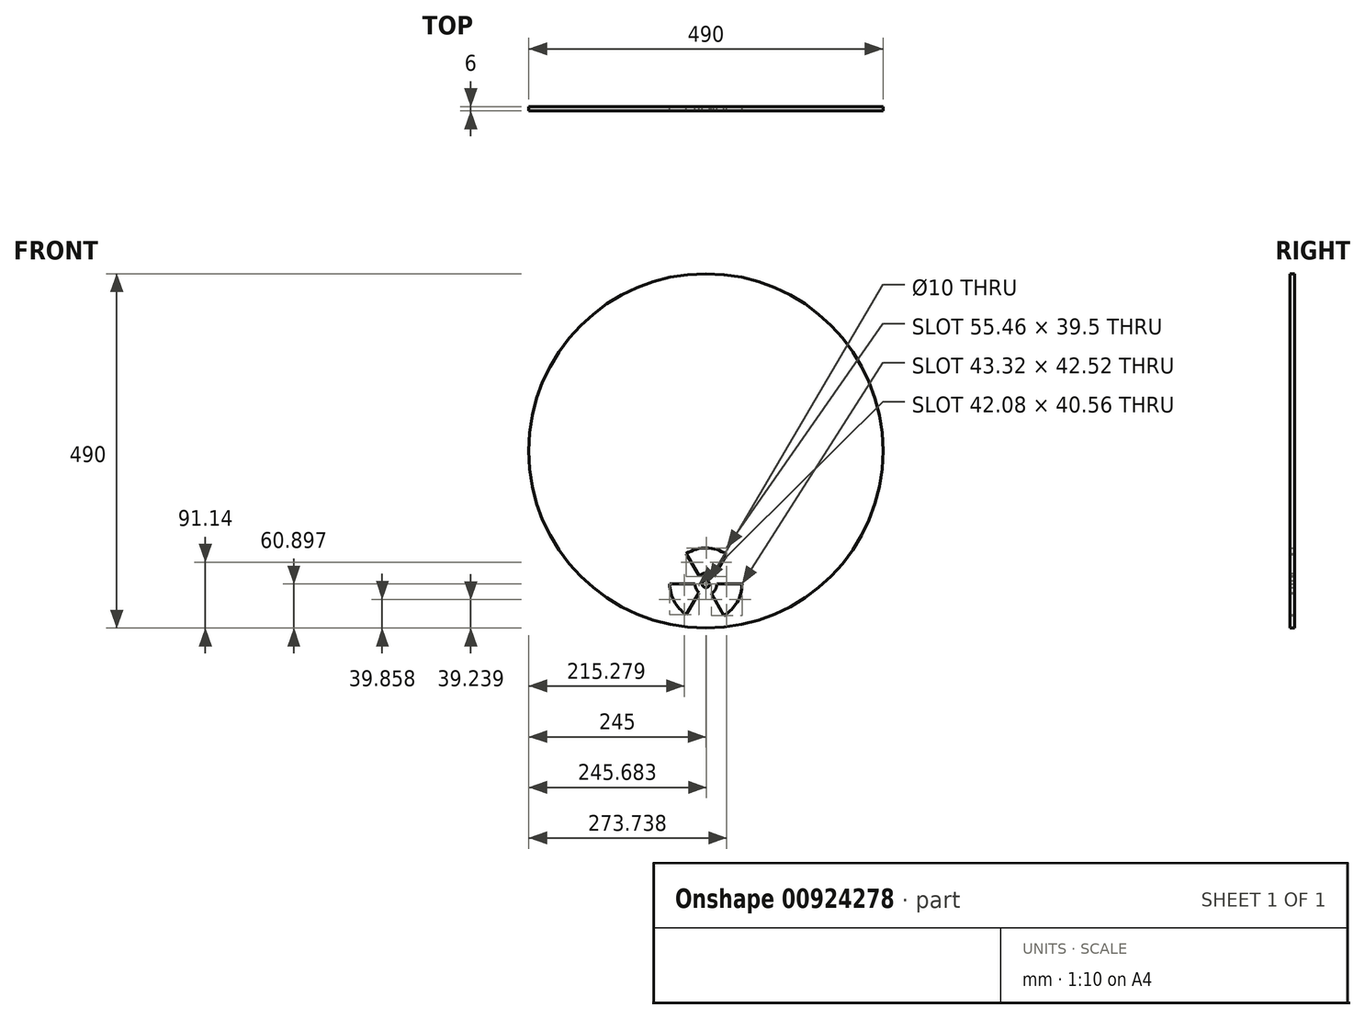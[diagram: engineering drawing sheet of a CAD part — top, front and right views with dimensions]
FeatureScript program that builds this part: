
annotation { "Feature Type Name" : "Feature", "Feature Type Description" : "" }
export const myFeature = defineFeature(function(context is Context, id is Id, definition is map)
    precondition{}
    {
        {
            var Q0;
            Q0=qCreatedBy(makeId("Front.planeOp"),FACE);
            var sketch = newSketch(context, id + "F0", { "sketchPlane" : qUnion([Q0])});
            skCircle(sketch, "E0", {"center": v(0, 0) * mm, "radius": 245 * mm});
            skArc(sketch, "E1", {"start": v(-27.05, -142.05) * mm, "mid": v(0.82, -134.1) * mm, "end": v(28.41, -142.96) * mm});
            skArc(sketch, "E2", {"start": v(50, -184.1) * mm, "mid": v(43.3, -209.11) * mm, "end": v(24.98, -227.42) * mm});
            skArc(sketch, "E3", {"start": v(-50, -184.1) * mm, "mid": v(-43.88, -208.08) * mm, "end": v(-27, -226.18) * mm});
            skArc(sketch, "E4", {"start": v(-15, -184.1) * mm, "mid": v(-13.54, -190.56) * mm, "end": v(-9.44, -195.76) * mm});
            skArc(sketch, "E5", {"start": v(15, -184.1) * mm, "mid": v(12.98, -191.61) * mm, "end": v(7.48, -197.1) * mm});
            skArc(sketch, "E6", {"start": v(-9.48, -172.48) * mm, "mid": v(0.84, -169.13) * mm, "end": v(10.72, -173.6) * mm});
            skLineSegment(sketch, "E7", {"start": v(-27.05, -142.05) * mm, "end": v(-9.48, -172.48) * mm});
            skLineSegment(sketch, "E8", {"start": v(10.72, -173.6) * mm, "end": v(28.41, -142.96) * mm});
            skLineSegment(sketch, "E9", {"start": v(50, -184.1) * mm, "end": v(15, -184.1) * mm});
            skLineSegment(sketch, "E10", {"start": v(7.48, -197.1) * mm, "end": v(24.98, -227.42) * mm});
            skLineSegment(sketch, "E11", {"start": v(-9.44, -195.76) * mm, "end": v(-27, -226.18) * mm});
            skLineSegment(sketch, "E12", {"start": v(-15, -184.1) * mm, "end": v(-50, -184.1) * mm});
            skCircle(sketch, "E13", {"center": v(0, -184.1) * mm, "radius": 5 * mm});
            skSolve(sketch);
        }
        {
            var Q0;
            Q0=makeQuery(id+"F0.imprint","IMPRINT",FACE,{"disambiguationData":[TD([[makeQuery(id+"F0.imprint","IMPRINT",EDGE,{"derivedFrom":sQuery(id+"F0.wireOp",EDGE,"E0")}),1.0]])]});
            extrude(context, id + "F1", {"entities" : qUnion([Q0]), "depth" : 6 * mm, "offsetDistance" : 25.4 * mm});
        }
    });
